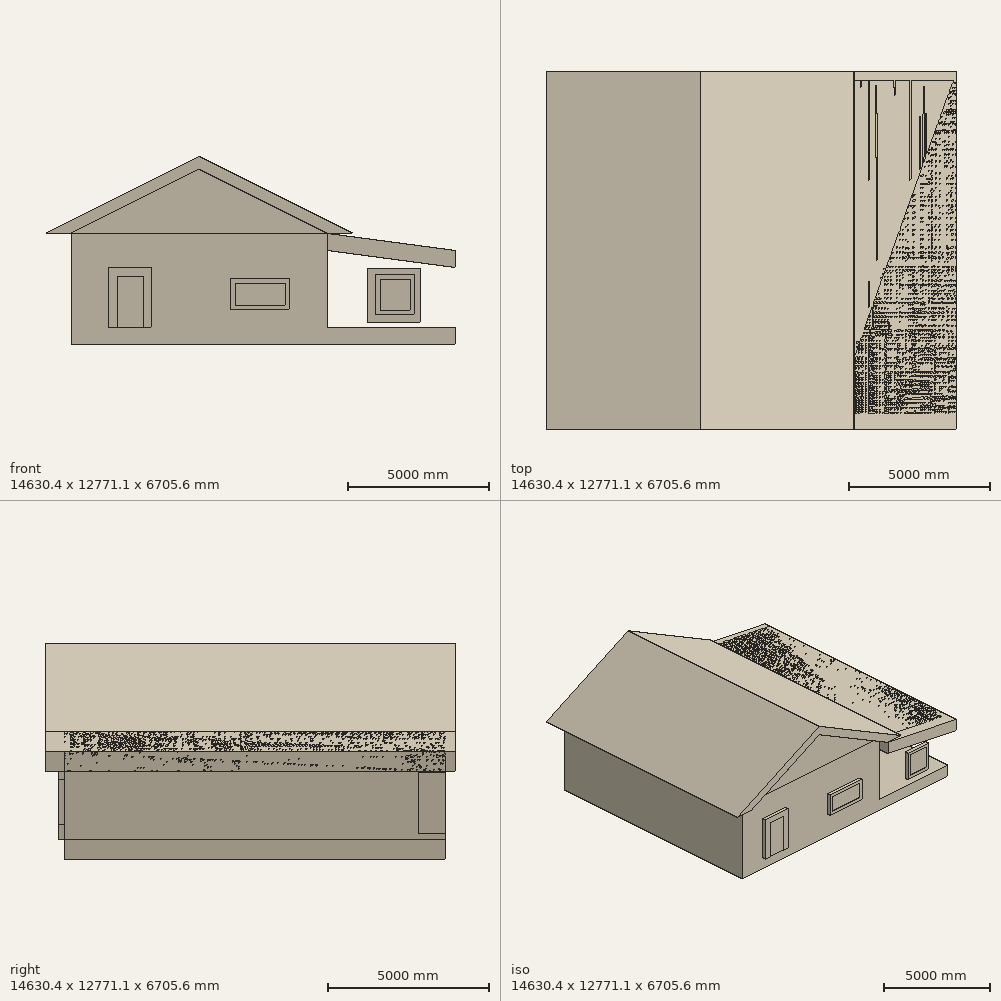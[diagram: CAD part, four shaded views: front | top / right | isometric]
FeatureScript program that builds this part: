
annotation { "Feature Type Name" : "Feature", "Feature Type Description" : "" }
export const myFeature = defineFeature(function(context is Context, id is Id, definition is map)
    precondition{}
    {
        {
            var Q0;
            Q0=qCreatedBy(makeId("Front.planeOp"),FACE);
            var sketch = newSketch(context, id + "F0", { "sketchPlane" : qUnion([Q0])});
            skLineSegment(sketch, "E0", {"start": v(0, 0) * mm, "end": v(0, 39.43) * mm});
            skLineSegment(sketch, "E1", {"start": v(0, 0) * mm, "end": v(-4572, 0) * mm});
            skLineSegment(sketch, "E2", {"start": v(0, 0) * mm, "end": v(4572, 0) * mm});
            skLineSegment(sketch, "E3", {"start": v(0.13, 2286) * mm, "end": v(4572, 0) * mm});
            skLineSegment(sketch, "E4", {"start": v(0.13, 2286) * mm, "end": v(-4572, 0) * mm});
            skLineSegment(sketch, "E5", {"start": v(0, 0) * mm, "end": v(0.13, 2286) * mm});
            skLineSegment(sketch, "E6", {"start": v(0.13, 2286) * mm, "end": v(0.13, 2743.2) * mm});
            skLineSegment(sketch, "E7", {"start": v(-4572, 0) * mm, "end": v(-5486.4, 0) * mm});
            skLineSegment(sketch, "E8", {"start": v(-5486.4, 0) * mm, "end": v(0.13, 2743.2) * mm});
            skLineSegment(sketch, "E9", {"start": v(4572, 0) * mm, "end": v(5486.4, 0) * mm});
            skLineSegment(sketch, "E10", {"start": v(5486.4, 0) * mm, "end": v(0.13, 2743.2) * mm});
            skLineSegment(sketch, "E11", {"start": v(-4572, 0) * mm, "end": v(-4572, -3352.8) * mm});
            skLineSegment(sketch, "E12", {"start": v(-4572, -3352.8) * mm, "end": v(4572, -3352.8) * mm});
            skLineSegment(sketch, "E13", {"start": v(4572, 0) * mm, "end": v(4572, -3352.8) * mm});
            skLineSegment(sketch, "E14", {"start": v(4572, -3352.8) * mm, "end": v(9144, -3352.8) * mm});
            skLineSegment(sketch, "E15", {"start": v(9144, -3352.8) * mm, "end": v(9144, -609.6) * mm});
            skLineSegment(sketch, "E16", {"start": v(9144, -609.6) * mm, "end": v(4572, 0) * mm});
            skLineSegment(sketch, "E17", {"start": v(4572, 0) * mm, "end": v(4572, -609.6) * mm});
            skLineSegment(sketch, "E18", {"start": v(9144, -609.6) * mm, "end": v(9144, -1219.2) * mm});
            skLineSegment(sketch, "E19", {"start": v(9144, -1219.2) * mm, "end": v(4572, -609.6) * mm});
            skLineSegment(sketch, "E20", {"start": v(-4572, -3352.8) * mm, "end": v(-4572, -3962.4) * mm});
            skLineSegment(sketch, "E21", {"start": v(4572, -3352.8) * mm, "end": v(4572, -3962.4) * mm});
            skLineSegment(sketch, "E22", {"start": v(4572, -3962.4) * mm, "end": v(-4572, -3962.4) * mm});
            skLineSegment(sketch, "E23", {"start": v(9144, -3352.8) * mm, "end": v(9144, -3962.4) * mm});
            skLineSegment(sketch, "E24", {"start": v(9144, -3962.4) * mm, "end": v(4572, -3962.4) * mm});
            skLineSegment(sketch, "E25", {"start": v(-2915.79, -3352.8) * mm, "end": v(-2915.79, -1524) * mm});
            skLineSegment(sketch, "E26", {"start": v(-2915.79, -1524) * mm, "end": v(-2001.39, -1524) * mm});
            skLineSegment(sketch, "E27", {"start": v(-2001.39, -1524) * mm, "end": v(-2001.39, -3352.8) * mm});
            skLineSegment(sketch, "E28", {"start": v(-2001.39, -3352.8) * mm, "end": v(-2915.79, -3352.8) * mm});
            skLineSegment(sketch, "E29.bottom", {"start": v(1276.33, -1775.54) * mm, "end": v(3083.8, -1775.54) * mm});
            skLineSegment(sketch, "E29.top", {"start": v(1276.33, -2576.86) * mm, "end": v(3083.8, -2576.86) * mm});
            skLineSegment(sketch, "E29.left", {"start": v(1276.33, -1775.54) * mm, "end": v(1276.33, -2576.86) * mm});
            skLineSegment(sketch, "E29.right", {"start": v(3083.8, -1775.54) * mm, "end": v(3083.8, -2576.86) * mm});
            skLineSegment(sketch, "E30.bottom", {"start": v(6456.24, -1626.62) * mm, "end": v(7536.9, -1626.62) * mm});
            skLineSegment(sketch, "E30.top", {"start": v(6456.24, -2744.55) * mm, "end": v(7536.9, -2744.55) * mm});
            skLineSegment(sketch, "E30.left", {"start": v(6456.24, -1626.62) * mm, "end": v(6456.24, -2744.55) * mm});
            skLineSegment(sketch, "E30.right", {"start": v(7536.9, -1626.62) * mm, "end": v(7536.9, -2744.55) * mm});
            skLineSegment(sketch, "E31.0", {"start": v(-1696.59, -1219.2) * mm, "end": v(-1696.59, -3352.8) * mm});
            skLineSegment(sketch, "E31.1", {"start": v(-3220.59, -1219.2) * mm, "end": v(-1696.59, -1219.2) * mm});
            skLineSegment(sketch, "E31.2", {"start": v(-3220.59, -3352.8) * mm, "end": v(-3220.59, -1219.2) * mm});
            skLineSegment(sketch, "E32.0", {"start": v(1123.93, -2729.26) * mm, "end": v(3236.2, -2729.26) * mm});
            skLineSegment(sketch, "E32.1", {"start": v(1123.93, -1623.14) * mm, "end": v(1123.93, -2729.26) * mm});
            skLineSegment(sketch, "E32.2", {"start": v(1123.93, -1623.14) * mm, "end": v(3236.2, -1623.14) * mm});
            skLineSegment(sketch, "E32.3", {"start": v(3236.2, -1623.14) * mm, "end": v(3236.2, -2729.26) * mm});
            skLineSegment(sketch, "E33.0", {"start": v(6303.84, -2896.95) * mm, "end": v(7689.3, -2896.95) * mm});
            skLineSegment(sketch, "E33.1", {"start": v(6303.84, -1474.22) * mm, "end": v(6303.84, -2896.95) * mm});
            skLineSegment(sketch, "E33.2", {"start": v(6303.84, -1474.22) * mm, "end": v(7689.3, -1474.22) * mm});
            skLineSegment(sketch, "E33.3", {"start": v(7689.3, -1474.22) * mm, "end": v(7689.3, -2896.95) * mm});
            skText(sketch, "E34", { "text": "Property of Reedy", "fontName": "OpenSans-Bold.ttf"});
            const initialGuessF0  = {"E34": [-7.59866, 3.6673, 1, 0, 1.1701]};
            skSetInitialGuess(sketch, initialGuessF0);
            skSolve(sketch);
        }
        {
            var Q0;
            Q0=makeQuery(id+"F0.imprint","IMPRINT",FACE,{"disambiguationData":[TD([[makeQuery(id+"F0.imprint","IMPRINT",EDGE,{"derivedFrom":sQuery(id+"F0.wireOp",EDGE,"E3")}),1.0]])]});
            var Q1;
            Q1=makeQuery(id+"F0.imprint","IMPRINT",FACE,{"disambiguationData":[TD([[makeQuery(id+"F0.imprint","IMPRINT",EDGE,{"derivedFrom":sQuery(id+"F0.wireOp",EDGE,"E4")}),-1.0]])]});
            var Q2;
            Q2=makeQuery(id+"F0.imprint","IMPRINT",FACE,{"disambiguationData":[TD([[makeQuery(id+"F0.imprint","IMPRINT",EDGE,{"derivedFrom":sQuery(id+"F0.wireOp",EDGE,"E16")}),1.0]])]});
            extrude(context, id + "F1", {"entities" : qUnion([Q0, Q1, Q2]), "oppositeDirection" : true, "depth" : 12192 * mm, "offsetDistance" : 30.48 * mm, "hasSecondDirection" : true, "secondDirectionOppositeDirection" : false, "secondDirectionDepth" : 579.12 * mm});
        }
        {
            var Q0;
            Q0=makeQuery(id+"F0.imprint","IMPRINT",FACE,{"disambiguationData":[TD([[makeQuery(id+"F0.imprint","IMPRINT",EDGE,{"derivedFrom":sQuery(id+"F0.wireOp",EDGE,"E2")}),1.0]])]});
            var Q1;
            Q1=makeQuery(id+"F0.imprint","IMPRINT",FACE,{"disambiguationData":[TD([[makeQuery(id+"F0.imprint","IMPRINT",EDGE,{"derivedFrom":sQuery(id+"F0.wireOp",EDGE,"E1")}),-1.0]])]});
            extrude(context, id + "F2", {"entities" : qUnion([Q0, Q1]), "operationType" : NewBodyOperationType.ADD, "oppositeDirection" : true, "depth" : 11887.2 * mm, "offsetDistance" : 30.48 * mm});
        }
        {
            var Q0;
            Q0=makeQuery(id+"F0.imprint","IMPRINT",FACE,{"disambiguationData":[TD([[makeQuery(id+"F0.imprint","IMPRINT",EDGE,{"derivedFrom":sQuery(id+"F0.wireOp",EDGE,"E1")}),1.0]])]});
            var Q1;
            {var subQ5=sQuery(id+"F0.wireOp",EDGE,"E20");Q1=makeQuery(id+"F0.imprint","IMPRINT",FACE,{"disambiguationData":[TD([[makeQuery(id+"F0.imprint","IMPRINT",EDGE,{"derivedFrom":subQ5}),1.0]])]});}
            var Q2;
            Q2=makeQuery(id+"F0.imprint","IMPRINT",FACE,{"disambiguationData":[TD([[makeQuery(id+"F0.imprint","IMPRINT",EDGE,{"derivedFrom":sQuery(id+"F0.wireOp",EDGE,"E14")}),-1.0]])]});
            var Q3;
            Q3=makeQuery(id+"F0.imprint","IMPRINT",FACE,{"disambiguationData":[TD([[makeQuery(id+"F0.imprint","IMPRINT",EDGE,{"derivedFrom":sQuery(id+"F0.wireOp",EDGE,"E13")}),1.0]])]});
            extrude(context, id + "F3", {"entities" : qUnion([Q0, Q1, Q2, Q3]), "oppositeDirection" : true, "depth" : 11887.2 * mm, "offsetDistance" : 30.48 * mm});
        }
        {
            var Q0;
            Q0=makeQuery(id+"F0.imprint","IMPRINT",FACE,{"disambiguationData":[TD([[makeQuery(id+"F0.imprint","IMPRINT",EDGE,{"derivedFrom":sQuery(id+"F0.wireOp",EDGE,"E25")}),-1.0]])]});
            var Q1;
            Q1=makeQuery(id+"F0.imprint","IMPRINT",FACE,{"disambiguationData":[TD([[makeQuery(id+"F0.imprint","IMPRINT",EDGE,{"derivedFrom":sQuery(id+"F0.wireOp",EDGE,"E29.bottom")}),-1.0]])]});
            var Q2;
            Q2=makeQuery(id+"F0.imprint","IMPRINT",FACE,{"disambiguationData":[TD([[makeQuery(id+"F0.imprint","IMPRINT",EDGE,{"derivedFrom":sQuery(id+"F0.wireOp",EDGE,"E30.bottom")}),-1.0]])]});
            extrude(context, id + "F4", {"entities" : qUnion([Q0, Q1, Q2]), "depth" : 152.4 * mm, "offsetDistance" : 30.48 * mm});
        }
        {
            var Q0;
            {var subQ4=sQuery(id+"F0.wireOp",EDGE,"E25");Q0=makeQuery(id+"F0.imprint","IMPRINT",FACE,{"disambiguationData":[TD([[makeQuery(id+"F0.imprint","IMPRINT",EDGE,{"derivedFrom":subQ4}),1.0]])]});}
            var Q1;
            Q1=makeQuery(id+"F0.imprint","IMPRINT",FACE,{"disambiguationData":[TD([[makeQuery(id+"F0.imprint","IMPRINT",EDGE,{"derivedFrom":sQuery(id+"F0.wireOp",EDGE,"E29.bottom")}),1.0]])]});
            var Q2;
            Q2=makeQuery(id+"F0.imprint","IMPRINT",FACE,{"disambiguationData":[TD([[makeQuery(id+"F0.imprint","IMPRINT",EDGE,{"derivedFrom":sQuery(id+"F0.wireOp",EDGE,"E30.bottom")}),1.0]])]});
            extrude(context, id + "F5", {"entities" : qUnion([Q0, Q1, Q2]), "depth" : 182.88 * mm, "offsetDistance" : 30.48 * mm});
        }
        {
            var Q0;
            Q0=makeQuery(id+"F3.opExtrude","CAP_FACE",FACE,{"disambiguationData":[OSD([sQuery(id+"F0.wireOp",EDGE,"E1"),sQuery(id+"F0.wireOp",EDGE,"E2"),sQuery(id+"F0.wireOp",EDGE,"E11"),sQuery(id+"F0.wireOp",EDGE,"E12"),sQuery(id+"F0.wireOp",EDGE,"E15"),sQuery(id+"F0.wireOp",EDGE,"E17"),sQuery(id+"F0.wireOp",EDGE,"E19"),sQuery(id+"F0.wireOp",EDGE,"E20"),sQuery(id+"F0.wireOp",EDGE,"E22"),sQuery(id+"F0.wireOp",EDGE,"E23"),sQuery(id+"F0.wireOp",EDGE,"E24"),sQuery(id+"F0.wireOp",EDGE,"E28"),sQuery(id+"F0.wireOp",EDGE,"E31.0"),sQuery(id+"F0.wireOp",EDGE,"E31.1"),sQuery(id+"F0.wireOp",EDGE,"E31.2"),sQuery(id+"F0.wireOp",EDGE,"E32.0"),sQuery(id+"F0.wireOp",EDGE,"E32.1"),sQuery(id+"F0.wireOp",EDGE,"E32.2"),sQuery(id+"F0.wireOp",EDGE,"E32.3"),sQuery(id+"F0.wireOp",EDGE,"E33.0"),sQuery(id+"F0.wireOp",EDGE,"E33.1"),sQuery(id+"F0.wireOp",EDGE,"E33.2"),sQuery(id+"F0.wireOp",EDGE,"E33.3")])],"isStart":false});
            var sketch = newSketch(context, id + "F6", { "sketchPlane" : qUnion([Q0])});
            skLineSegment(sketch, "E35.bottom", {"start": v(-7902.42, -1268.34) * mm, "end": v(-6018.41, -1268.34) * mm});
            skLineSegment(sketch, "E35.top", {"start": v(-7902.42, -3178.7) * mm, "end": v(-6018.41, -3178.7) * mm});
            skLineSegment(sketch, "E35.left", {"start": v(-7902.42, -1268.34) * mm, "end": v(-7902.42, -3178.7) * mm});
            skLineSegment(sketch, "E35.right", {"start": v(-6018.41, -1268.34) * mm, "end": v(-6018.41, -3178.7) * mm});
            skLineSegment(sketch, "E36.bottom", {"start": v(-3436.12, -1202.6) * mm, "end": v(-853.86, -1202.6) * mm});
            skLineSegment(sketch, "E36.top", {"start": v(-3436.12, -3046.95) * mm, "end": v(-853.86, -3046.95) * mm});
            skLineSegment(sketch, "E36.left", {"start": v(-3436.12, -1202.6) * mm, "end": v(-3436.12, -3046.95) * mm});
            skLineSegment(sketch, "E36.right", {"start": v(-853.86, -1202.6) * mm, "end": v(-853.86, -3046.95) * mm});
            skLineSegment(sketch, "E37.bottom", {"start": v(1465.08, -814.2) * mm, "end": v(3514.25, -814.2) * mm});
            skLineSegment(sketch, "E37.top", {"start": v(1465.08, -3667.74) * mm, "end": v(3514.25, -3667.74) * mm});
            skLineSegment(sketch, "E37.left", {"start": v(1465.08, -814.2) * mm, "end": v(1465.08, -3667.74) * mm});
            skLineSegment(sketch, "E37.right", {"start": v(3514.25, -814.2) * mm, "end": v(3514.25, -3667.74) * mm});
            skSolve(sketch);
        }
        {
            var Q0;
            Q0 = qSketchRegion(id + "F6", true);
            extrude(context, id + "F7", {"entities" : qUnion([Q0]), "operationType" : NewBodyOperationType.ADD, "oppositeDirection" : true, "depth" : 853.44 * mm, "offsetDistance" : 30.48 * mm});
        }
        {
            var Q0;
            Q0=makeQuery(id+"F6.imprint","IMPRINT",FACE,{"disambiguationData":[TD([[makeQuery(id+"F6.imprint","IMPRINT",EDGE,{"derivedFrom":sQuery(id+"F6.wireOp",EDGE,"E36.bottom")}),-1.0]])]});
            extrude(context, id + "F8", {"entities" : qUnion([Q0]), "operationType" : NewBodyOperationType.ADD, "oppositeDirection" : true, "depth" : 1767.84 * mm, "offsetDistance" : 30.48 * mm});
        }
        {
            var Q0;
            Q0=makeQuery(id+"F6.imprint","IMPRINT",FACE,{"disambiguationData":[TD([[makeQuery(id+"F6.imprint","IMPRINT",EDGE,{"derivedFrom":sQuery(id+"F6.wireOp",EDGE,"E37.bottom")}),-1.0]])]});
            extrude(context, id + "F9", {"entities" : qUnion([Q0]), "operationType" : NewBodyOperationType.ADD, "oppositeDirection" : true, "depth" : 1798.32 * mm, "offsetDistance" : 30.48 * mm});
        }
    });
